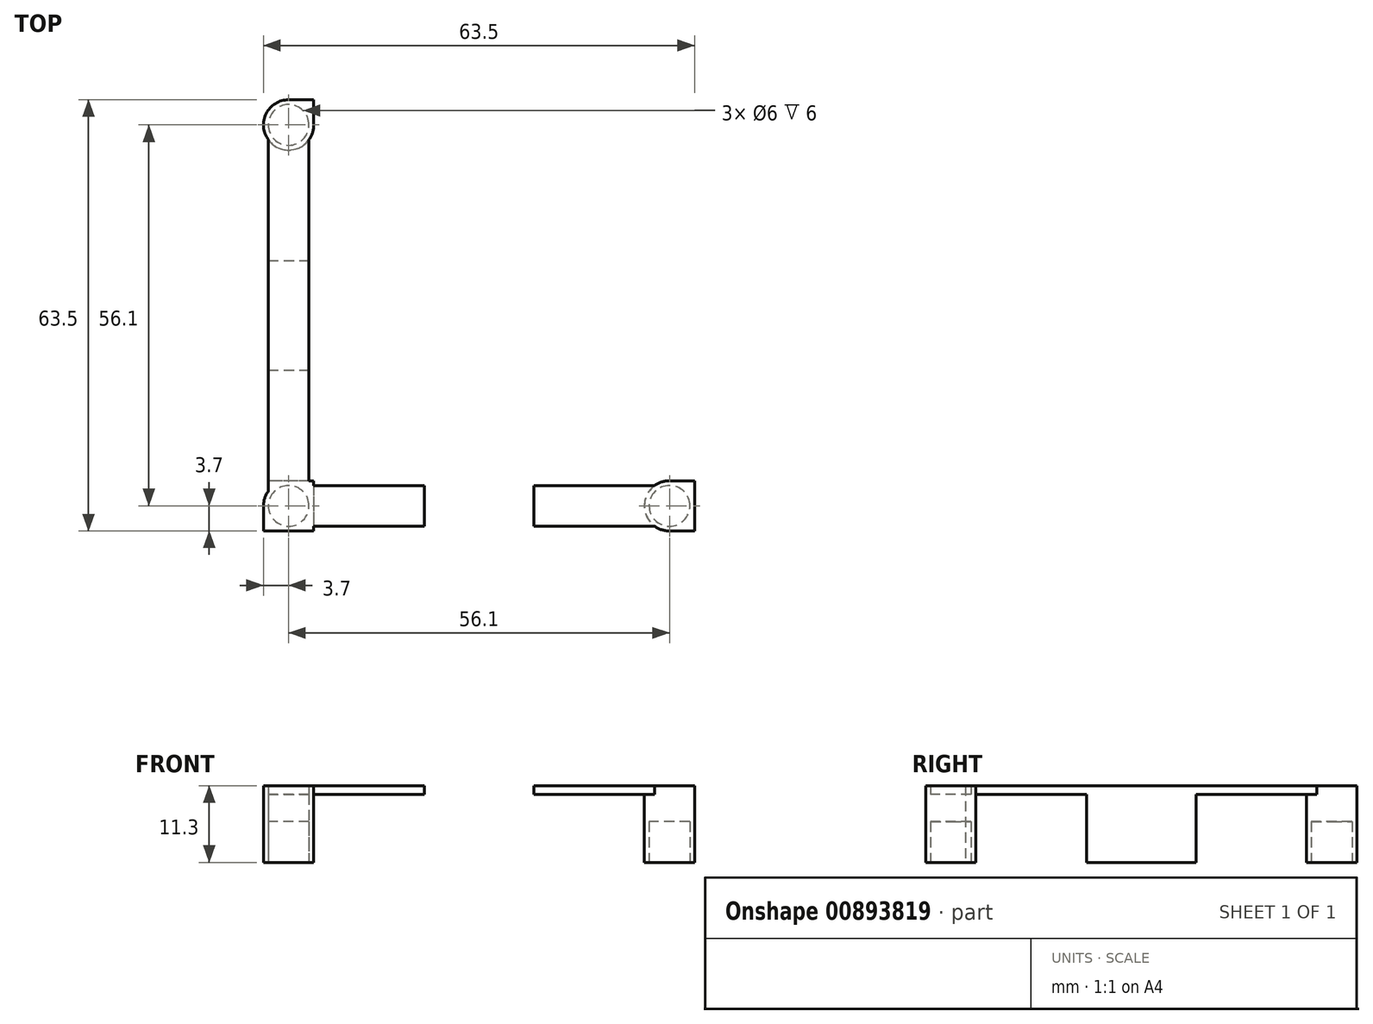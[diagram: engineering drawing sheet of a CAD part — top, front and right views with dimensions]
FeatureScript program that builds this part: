
annotation { "Feature Type Name" : "Feature", "Feature Type Description" : "" }
export const myFeature = defineFeature(function(context is Context, id is Id, definition is map)
    precondition{}
    {
        {
            var Q0;
            Q0=qCreatedBy(makeId("Top.planeOp"),FACE);
            var sketch = newSketch(context, id + "F0", { "sketchPlane" : qUnion([Q0])});
            skLineSegment(sketch, "E0.bottom", {"start": v(0, 0) * mm, "end": v(63.5, 0) * mm});
            skLineSegment(sketch, "E0.top", {"start": v(0, 63.5) * mm, "end": v(63.5, 63.5) * mm, "construction": true});
            skLineSegment(sketch, "E0.left", {"start": v(0, 0) * mm, "end": v(0, 63.5) * mm});
            skLineSegment(sketch, "E0.right", {"start": v(63.5, 0) * mm, "end": v(63.5, 63.5) * mm, "construction": true});
            skLineSegment(sketch, "E1", {"start": v(0, 63.5) * mm, "end": v(0, 0) * mm});
            skLineSegment(sketch, "E2.0", {"start": v(7.4, 7.4) * mm, "end": v(63.5, 7.4) * mm});
            skLineSegment(sketch, "E2.1", {"start": v(7.4, 63.5) * mm, "end": v(7.4, 7.4) * mm});
            skLineSegment(sketch, "E3", {"start": v(63.5, 7.4) * mm, "end": v(63.5, 0) * mm});
            skLineSegment(sketch, "E4", {"start": v(7.4, 63.5) * mm, "end": v(0, 63.5) * mm});
            skCircle(sketch, "E5", {"center": v(3.7, 59.8) * mm, "radius": 3 * mm});
            skCircle(sketch, "E6", {"center": v(59.8, 3.7) * mm, "radius": 3 * mm});
            skCircle(sketch, "E7", {"center": v(3.7, 3.7) * mm, "radius": 3 * mm});
            skLineSegment(sketch, "E8", {"start": v(3.7, 59.8) * mm, "end": v(7.4, 59.8) * mm, "construction": true});
            skLineSegment(sketch, "E9", {"start": v(7.4, 59.8) * mm, "end": v(0, 59.8) * mm, "construction": true});
            skLineSegment(sketch, "E10", {"start": v(3.7, 3.7) * mm, "end": v(3.7, 0) * mm, "construction": true});
            skLineSegment(sketch, "E11", {"start": v(3.7, 0) * mm, "end": v(3.7, 3.7) * mm, "construction": true});
            skLineSegment(sketch, "E12", {"start": v(3.7, 3.7) * mm, "end": v(0, 3.7) * mm, "construction": true});
            skLineSegment(sketch, "E13", {"start": v(3.7, 3.7) * mm, "end": v(6.7, 3.7) * mm, "construction": true});
            skLineSegment(sketch, "E14", {"start": v(59.8, 3.7) * mm, "end": v(59.8, 7.4) * mm, "construction": true});
            skLineSegment(sketch, "E15", {"start": v(59.8, 7.4) * mm, "end": v(59.8, 0) * mm, "construction": true});
            skLineSegment(sketch, "E16", {"start": v(3.7, 3.7) * mm, "end": v(3.7, 6.7) * mm, "construction": true});
            skLineSegment(sketch, "E17", {"start": v(59.8, 0.7) * mm, "end": v(3.7, 0.7) * mm});
            skLineSegment(sketch, "E18", {"start": v(59.8, 6.7) * mm, "end": v(3.7, 6.7) * mm});
            skLineSegment(sketch, "E19", {"start": v(6.7, 3.7) * mm, "end": v(6.7, 59.8) * mm});
            skLineSegment(sketch, "E20", {"start": v(0.7, 59.8) * mm, "end": v(0.7, 3.7) * mm});
            skLineSegment(sketch, "E21.bottom", {"start": v(0.7, 39.8) * mm, "end": v(6.7, 39.8) * mm});
            skLineSegment(sketch, "E21.top", {"start": v(0.7, 23.7) * mm, "end": v(6.7, 23.7) * mm});
            skLineSegment(sketch, "E21.left", {"start": v(0.7, 39.8) * mm, "end": v(0.7, 23.7) * mm});
            skLineSegment(sketch, "E21.right", {"start": v(6.7, 39.8) * mm, "end": v(6.7, 23.7) * mm});
            skLineSegment(sketch, "E22.bottom", {"start": v(23.7, 6.7) * mm, "end": v(39.8, 6.7) * mm});
            skLineSegment(sketch, "E22.top", {"start": v(23.7, 0.7) * mm, "end": v(39.8, 0.7) * mm});
            skLineSegment(sketch, "E22.left", {"start": v(23.7, 6.7) * mm, "end": v(23.7, 0.7) * mm});
            skLineSegment(sketch, "E22.right", {"start": v(39.8, 6.7) * mm, "end": v(39.8, 0.7) * mm});
            skCircle(sketch, "E23", {"center": v(3.7, 59.8) * mm, "radius": 3.7 * mm});
            skCircle(sketch, "E24", {"center": v(3.7, 3.7) * mm, "radius": 3.7 * mm});
            skCircle(sketch, "E25", {"center": v(59.8, 3.7) * mm, "radius": 3.7 * mm});
            skLineSegment(sketch, "E26", {"start": v(6.7, 3.7) * mm, "end": v(7.4, 3.7) * mm, "construction": true});
            skLineSegment(sketch, "E27", {"start": v(3.7, 6.7) * mm, "end": v(3.7, 7.4) * mm, "construction": true});
            skLineSegment(sketch, "E28", {"start": v(7.4, 7.4) * mm, "end": v(0, 7.4) * mm});
            skLineSegment(sketch, "E29", {"start": v(7.4, 7.4) * mm, "end": v(7.4, 0) * mm});
            skSolve(sketch);
        }
        {
            var Q0;
            {var subQ0=sQuery(id+"F0.wireOp",EDGE,"E6");var subQ1=makeQuery(id+"F0.imprint","INTERSECT",VERTEX,{"derivedFrom":[subQ0,sQuery(id+"F0.wireOp",EDGE,"E17")]});Q0=makeQuery(id+"F0.imprint","IMPRINT",FACE,{"disambiguationData":[TD([[makeQuery(id+"F0.imprint","IMPRINT",EDGE,{"disambiguationData":[TD([[subQ1,1.0]])],"derivedFrom":subQ0}),1.0]])]});}
            var Q1;
            {var subQ0=sQuery(id+"F0.wireOp",EDGE,"E22.top");Q1=makeQuery(id+"F0.imprint","IMPRINT",FACE,{"disambiguationData":[TD([[makeQuery(id+"F0.imprint","IMPRINT",EDGE,{"derivedFrom":subQ0}),-1.0]])]});}
            var Q2;
            {var subQ4=sQuery(id+"F0.wireOp",EDGE,"E7");var subQ6=sQuery(id+"F0.wireOp",EDGE,"E17");var subQ7=makeQuery(id+"F0.imprint","INTERSECT",VERTEX,{"derivedFrom":[subQ4,subQ6]});Q2=makeQuery(id+"F0.imprint","IMPRINT",FACE,{"disambiguationData":[TD([[makeQuery(id+"F0.imprint","IMPRINT",EDGE,{"disambiguationData":[TD([[subQ7,-1.0]])],"derivedFrom":subQ4}),-1.0]])]});}
            var Q3;
            {var subQ0=sQuery(id+"F0.wireOp",EDGE,"E19");var subQ1=sQuery(id+"F0.wireOp",EDGE,"E5");var subQ2=makeQuery(id+"F0.imprint","INTERSECT",VERTEX,{"derivedFrom":[subQ1,subQ0]});Q3=makeQuery(id+"F0.imprint","IMPRINT",FACE,{"disambiguationData":[TD([[makeQuery(id+"F0.imprint","IMPRINT",EDGE,{"disambiguationData":[TD([[subQ2,1.0]])],"derivedFrom":subQ1}),-1.0]])]});}
            var Q4;
            {var subQ0=sQuery(id+"F0.wireOp",EDGE,"E21.top");Q4=makeQuery(id+"F0.imprint","IMPRINT",FACE,{"disambiguationData":[TD([[makeQuery(id+"F0.imprint","IMPRINT",EDGE,{"derivedFrom":subQ0}),-1.0]])]});}
            var Q5;
            {var subQ0=sQuery(id+"F0.wireOp",EDGE,"E22.right");Q5=makeQuery(id+"F0.imprint","IMPRINT",FACE,{"disambiguationData":[TD([[makeQuery(id+"F0.imprint","IMPRINT",EDGE,{"derivedFrom":subQ0}),1.0]])]});}
            var Q6;
            {var subQ0=sQuery(id+"F0.wireOp",EDGE,"E18");var subQ1=sQuery(id+"F0.wireOp",EDGE,"E7");var subQ2=makeQuery(id+"F0.imprint","INTERSECT",VERTEX,{"derivedFrom":[subQ1,subQ0]});Q6=makeQuery(id+"F0.imprint","IMPRINT",FACE,{"disambiguationData":[TD([[makeQuery(id+"F0.imprint","IMPRINT",EDGE,{"disambiguationData":[TD([[subQ2,1.0]])],"derivedFrom":subQ1}),-1.0]])]});}
            var Q7;
            {var subQ0=sQuery(id+"F0.wireOp",EDGE,"E21.right");Q7=makeQuery(id+"F0.imprint","IMPRINT",FACE,{"disambiguationData":[TD([[makeQuery(id+"F0.imprint","IMPRINT",EDGE,{"derivedFrom":subQ0}),1.0]])]});}
            var Q8;
            {var subQ4=sQuery(id+"F0.wireOp",EDGE,"E6");var subQ7=sQuery(id+"F0.wireOp",EDGE,"E17");var subQ8=makeQuery(id+"F0.imprint","INTERSECT",VERTEX,{"derivedFrom":[subQ4,subQ7]});Q8=makeQuery(id+"F0.imprint","IMPRINT",FACE,{"disambiguationData":[TD([[makeQuery(id+"F0.imprint","IMPRINT",EDGE,{"disambiguationData":[TD([[subQ8,-1.0]])],"derivedFrom":subQ4}),-1.0]])]});}
            var Q9;
            {var subQ0=sQuery(id+"F0.wireOp",EDGE,"E4");var subQ1=sQuery(id+"F0.wireOp",EDGE,"E1");var subQ2=makeQuery(id+"F0.imprint","INTERSECT",VERTEX,{"derivedFrom":[subQ1,subQ0]});Q9=makeQuery(id+"F0.imprint","IMPRINT",FACE,{"disambiguationData":[TD([[makeQuery(id+"F0.imprint","IMPRINT",EDGE,{"disambiguationData":[TD([[subQ2,-1.0]])],"derivedFrom":subQ1}),1.0]])]});}
            var Q10;
            {var subQ0=sQuery(id+"F0.wireOp",EDGE,"E3");var subQ1=sQuery(id+"F0.wireOp",EDGE,"E0.bottom");var subQ2=makeQuery(id+"F0.imprint","INTERSECT",VERTEX,{"derivedFrom":[subQ1,subQ0]});Q10=makeQuery(id+"F0.imprint","IMPRINT",FACE,{"disambiguationData":[TD([[makeQuery(id+"F0.imprint","IMPRINT",EDGE,{"disambiguationData":[TD([[subQ2,1.0]])],"derivedFrom":subQ1}),1.0]])]});}
            var Q11;
            {var subQ0=sQuery(id+"F0.wireOp",EDGE,"E4");var subQ1=sQuery(id+"F0.wireOp",EDGE,"E2.1");var subQ2=makeQuery(id+"F0.imprint","INTERSECT",VERTEX,{"derivedFrom":[subQ1,subQ0]});Q11=makeQuery(id+"F0.imprint","IMPRINT",FACE,{"disambiguationData":[TD([[makeQuery(id+"F0.imprint","IMPRINT",EDGE,{"disambiguationData":[TD([[subQ2,-1.0]])],"derivedFrom":subQ1}),-1.0]])]});}
            var Q12;
            {var subQ0=sQuery(id+"F0.wireOp",EDGE,"E3");var subQ1=sQuery(id+"F0.wireOp",EDGE,"E2.0");var subQ2=makeQuery(id+"F0.imprint","INTERSECT",VERTEX,{"derivedFrom":[subQ1,subQ0]});Q12=makeQuery(id+"F0.imprint","IMPRINT",FACE,{"disambiguationData":[TD([[makeQuery(id+"F0.imprint","IMPRINT",EDGE,{"disambiguationData":[TD([[subQ2,1.0]])],"derivedFrom":subQ1}),-1.0]])]});}
            var Q13;
            {var subQ0=sQuery(id+"F0.wireOp",EDGE,"E21.left");Q13=makeQuery(id+"F0.imprint","IMPRINT",FACE,{"disambiguationData":[TD([[makeQuery(id+"F0.imprint","IMPRINT",EDGE,{"derivedFrom":subQ0}),-1.0]])]});}
            var Q14;
            {var subQ0=sQuery(id+"F0.wireOp",EDGE,"E17");var subQ1=sQuery(id+"F0.wireOp",EDGE,"E6");var subQ2=makeQuery(id+"F0.imprint","INTERSECT",VERTEX,{"derivedFrom":[subQ1,subQ0]});Q14=makeQuery(id+"F0.imprint","IMPRINT",FACE,{"disambiguationData":[TD([[makeQuery(id+"F0.imprint","IMPRINT",EDGE,{"disambiguationData":[TD([[subQ2,1.0]])],"derivedFrom":subQ1}),-1.0]])]});}
            var Q15;
            {var subQ0=sQuery(id+"F0.wireOp",EDGE,"E21.bottom");Q15=makeQuery(id+"F0.imprint","IMPRINT",FACE,{"disambiguationData":[TD([[makeQuery(id+"F0.imprint","IMPRINT",EDGE,{"derivedFrom":subQ0}),1.0]])]});}
            var Q16;
            {var subQ4=sQuery(id+"F0.wireOp",EDGE,"E22.left");Q16=makeQuery(id+"F0.imprint","IMPRINT",FACE,{"disambiguationData":[TD([[makeQuery(id+"F0.imprint","IMPRINT",EDGE,{"derivedFrom":subQ4}),-1.0]])]});}
            var Q17;
            {var subQ1=sQuery(id+"F0.wireOp",EDGE,"E7");var subQ5=sQuery(id+"F0.wireOp",EDGE,"E18");var subQ6=makeQuery(id+"F0.imprint","INTERSECT",VERTEX,{"derivedFrom":[subQ1,subQ5]});Q17=makeQuery(id+"F0.imprint","IMPRINT",FACE,{"disambiguationData":[TD([[makeQuery(id+"F0.imprint","IMPRINT",EDGE,{"disambiguationData":[TD([[subQ6,-1.0]])],"derivedFrom":subQ1}),-1.0]])]});}
            var Q18;
            Q18=makeQuery(id+"F0.imprint","IMPRINT",FACE,{"disambiguationData":[TD([[makeQuery(id+"F0.imprint","IMPRINT",EDGE,{"derivedFrom":sQuery(id+"F0.wireOp",EDGE,"E22.bottom")}),-1.0]])]});
            var Q19;
            {var subQ0=sQuery(id+"F0.wireOp",EDGE,"E5");var subQ1=makeQuery(id+"F0.imprint","INTERSECT",VERTEX,{"derivedFrom":[subQ0,sQuery(id+"F0.wireOp",EDGE,"E19")]});Q19=makeQuery(id+"F0.imprint","IMPRINT",FACE,{"disambiguationData":[TD([[makeQuery(id+"F0.imprint","IMPRINT",EDGE,{"disambiguationData":[TD([[subQ1,-1.0]])],"derivedFrom":subQ0}),1.0]])]});}
            var Q20;
            {var subQ1=sQuery(id+"F0.wireOp",EDGE,"E7");var subQ6=sQuery(id+"F0.wireOp",EDGE,"E17");var subQ7=makeQuery(id+"F0.imprint","INTERSECT",VERTEX,{"derivedFrom":[subQ1,subQ6]});Q20=makeQuery(id+"F0.imprint","IMPRINT",FACE,{"disambiguationData":[TD([[makeQuery(id+"F0.imprint","IMPRINT",EDGE,{"disambiguationData":[TD([[subQ7,1.0]])],"derivedFrom":subQ1}),-1.0]])]});}
            var Q21;
            {var subQ3=sQuery(id+"F0.wireOp",EDGE,"E19");var subQ4=sQuery(id+"F0.wireOp",EDGE,"E5");var subQ5=makeQuery(id+"F0.imprint","INTERSECT",VERTEX,{"derivedFrom":[subQ4,subQ3]});Q21=makeQuery(id+"F0.imprint","IMPRINT",FACE,{"disambiguationData":[TD([[makeQuery(id+"F0.imprint","IMPRINT",EDGE,{"disambiguationData":[TD([[subQ5,-1.0]])],"derivedFrom":subQ4}),-1.0]])]});}
            var Q22;
            Q22=makeQuery(id+"F0.imprint","IMPRINT",FACE,{"disambiguationData":[TD([[makeQuery(id+"F0.imprint","IMPRINT",EDGE,{"derivedFrom":sQuery(id+"F0.wireOp",EDGE,"E21.bottom")}),-1.0]])]});
            var Q23;
            {var subQ0=sQuery(id+"F0.wireOp",EDGE,"E7");var subQ1=makeQuery(id+"F0.imprint","INTERSECT",VERTEX,{"derivedFrom":[subQ0,sQuery(id+"F0.wireOp",EDGE,"E18")]});Q23=makeQuery(id+"F0.imprint","IMPRINT",FACE,{"disambiguationData":[TD([[makeQuery(id+"F0.imprint","IMPRINT",EDGE,{"disambiguationData":[TD([[subQ1,1.0]])],"derivedFrom":subQ0}),1.0]])]});}
            var Q24;
            {var subQ0=sQuery(id+"F0.wireOp",EDGE,"E1");var subQ1=sQuery(id+"F0.wireOp",EDGE,"E0.bottom");var subQ2=makeQuery(id+"F0.imprint","INTERSECT",VERTEX,{"derivedFrom":[subQ1,subQ0]});Q24=makeQuery(id+"F0.imprint","IMPRINT",FACE,{"disambiguationData":[TD([[makeQuery(id+"F0.imprint","IMPRINT",EDGE,{"disambiguationData":[TD([[subQ2,-1.0]])],"derivedFrom":subQ1}),1.0]])]});}
            var Q25;
            {var subQ0=sQuery(id+"F0.wireOp",EDGE,"E19");var subQ1=sQuery(id+"F0.wireOp",EDGE,"E18");var subQ2=makeQuery(id+"F0.imprint","INTERSECT",VERTEX,{"derivedFrom":[subQ1,subQ0]});Q25=makeQuery(id+"F0.imprint","IMPRINT",FACE,{"disambiguationData":[TD([[makeQuery(id+"F0.imprint","IMPRINT",EDGE,{"disambiguationData":[TD([[subQ2,-1.0]])],"derivedFrom":subQ1}),1.0]])]});}
            var Q26;
            {var subQ0=sQuery(id+"F0.wireOp",EDGE,"E22.bottom");Q26=makeQuery(id+"F0.imprint","IMPRINT",FACE,{"disambiguationData":[TD([[makeQuery(id+"F0.imprint","IMPRINT",EDGE,{"derivedFrom":subQ0}),1.0]])]});}
            var Q27;
            {var subQ0=sQuery(id+"F0.wireOp",EDGE,"E29");var subQ1=sQuery(id+"F0.wireOp",EDGE,"E0.bottom");var subQ2=makeQuery(id+"F0.imprint","INTERSECT",VERTEX,{"derivedFrom":[subQ1,subQ0]});Q27=makeQuery(id+"F0.imprint","IMPRINT",FACE,{"disambiguationData":[TD([[makeQuery(id+"F0.imprint","IMPRINT",EDGE,{"disambiguationData":[TD([[subQ2,1.0]])],"derivedFrom":subQ1}),1.0]])]});}
            var Q28;
            {var subQ0=sQuery(id+"F0.wireOp",EDGE,"E28");var subQ1=sQuery(id+"F0.wireOp",EDGE,"E20");var subQ2=makeQuery(id+"F0.imprint","INTERSECT",VERTEX,{"derivedFrom":[subQ1,subQ0]});Q28=makeQuery(id+"F0.imprint","IMPRINT",FACE,{"disambiguationData":[TD([[makeQuery(id+"F0.imprint","IMPRINT",EDGE,{"disambiguationData":[TD([[subQ2,-1.0]])],"derivedFrom":subQ1}),1.0]])]});}
            var Q29;
            {var subQ0=sQuery(id+"F0.wireOp",EDGE,"E28");var subQ1=sQuery(id+"F0.wireOp",EDGE,"E1");var subQ2=makeQuery(id+"F0.imprint","INTERSECT",VERTEX,{"derivedFrom":[subQ1,subQ0]});Q29=makeQuery(id+"F0.imprint","IMPRINT",FACE,{"disambiguationData":[TD([[makeQuery(id+"F0.imprint","IMPRINT",EDGE,{"disambiguationData":[TD([[subQ2,-1.0]])],"derivedFrom":subQ1}),1.0]])]});}
            var Q30;
            {var subQ0=sQuery(id+"F0.wireOp",EDGE,"E19");var subQ1=sQuery(id+"F0.wireOp",EDGE,"E18");var subQ2=makeQuery(id+"F0.imprint","INTERSECT",VERTEX,{"derivedFrom":[subQ1,subQ0]});Q30=makeQuery(id+"F0.imprint","IMPRINT",FACE,{"disambiguationData":[TD([[makeQuery(id+"F0.imprint","IMPRINT",EDGE,{"disambiguationData":[TD([[subQ2,-1.0]])],"derivedFrom":subQ1}),-1.0]])]});}
            var Q31;
            {var subQ0=sQuery(id+"F0.wireOp",EDGE,"E29");var subQ1=sQuery(id+"F0.wireOp",EDGE,"E17");var subQ2=makeQuery(id+"F0.imprint","INTERSECT",VERTEX,{"derivedFrom":[subQ1,subQ0]});Q31=makeQuery(id+"F0.imprint","IMPRINT",FACE,{"disambiguationData":[TD([[makeQuery(id+"F0.imprint","IMPRINT",EDGE,{"disambiguationData":[TD([[subQ2,-1.0]])],"derivedFrom":subQ1}),-1.0]])]});}
            var Q32;
            {var subQ0=sQuery(id+"F0.wireOp",EDGE,"E29");var subQ1=sQuery(id+"F0.wireOp",EDGE,"E18");var subQ2=makeQuery(id+"F0.imprint","INTERSECT",VERTEX,{"derivedFrom":[subQ1,subQ0]});Q32=makeQuery(id+"F0.imprint","IMPRINT",FACE,{"disambiguationData":[TD([[makeQuery(id+"F0.imprint","IMPRINT",EDGE,{"disambiguationData":[TD([[subQ2,-1.0]])],"derivedFrom":subQ1}),1.0]])]});}
            var Q33;
            {var subQ0=sQuery(id+"F0.wireOp",EDGE,"E29");var subQ1=sQuery(id+"F0.wireOp",EDGE,"E18");var subQ2=makeQuery(id+"F0.imprint","INTERSECT",VERTEX,{"derivedFrom":[subQ1,subQ0]});Q33=makeQuery(id+"F0.imprint","IMPRINT",FACE,{"disambiguationData":[TD([[makeQuery(id+"F0.imprint","IMPRINT",EDGE,{"disambiguationData":[TD([[subQ2,-1.0]])],"derivedFrom":subQ1}),-1.0]])]});}
            extrude(context, id + "F1", {"entities" : qUnion([Q0, Q1, Q2, Q3, Q4, Q5, Q6, Q7, Q8, Q9, Q10, Q11, Q12, Q13, Q14, Q15, Q16, Q17, Q18, Q19, Q20, Q21, Q22, Q23, Q24, Q25, Q26, Q27, Q28, Q29, Q30, Q31, Q32, Q33]), "depth" : 11.3 * mm, "offsetDistance" : 25 * mm});
        }
        {
            var Q0;
            {var subQ0=sQuery(id+"F0.wireOp",EDGE,"E5");var subQ1=makeQuery(id+"F0.imprint","INTERSECT",VERTEX,{"derivedFrom":[subQ0,sQuery(id+"F0.wireOp",EDGE,"E19")]});Q0=makeQuery(id+"F0.imprint","IMPRINT",FACE,{"disambiguationData":[TD([[makeQuery(id+"F0.imprint","IMPRINT",EDGE,{"disambiguationData":[TD([[subQ1,-1.0]])],"derivedFrom":subQ0}),1.0]])]});}
            var Q1;
            {var subQ0=sQuery(id+"F0.wireOp",EDGE,"E7");var subQ1=makeQuery(id+"F0.imprint","INTERSECT",VERTEX,{"derivedFrom":[subQ0,sQuery(id+"F0.wireOp",EDGE,"E18")]});Q1=makeQuery(id+"F0.imprint","IMPRINT",FACE,{"disambiguationData":[TD([[makeQuery(id+"F0.imprint","IMPRINT",EDGE,{"disambiguationData":[TD([[subQ1,1.0]])],"derivedFrom":subQ0}),1.0]])]});}
            var Q2;
            {var subQ0=sQuery(id+"F0.wireOp",EDGE,"E6");var subQ1=makeQuery(id+"F0.imprint","INTERSECT",VERTEX,{"derivedFrom":[subQ0,sQuery(id+"F0.wireOp",EDGE,"E17")]});Q2=makeQuery(id+"F0.imprint","IMPRINT",FACE,{"disambiguationData":[TD([[makeQuery(id+"F0.imprint","IMPRINT",EDGE,{"disambiguationData":[TD([[subQ1,1.0]])],"derivedFrom":subQ0}),1.0]])]});}
            extrude(context, id + "F2", {"entities" : qUnion([Q0, Q1, Q2]), "operationType" : NewBodyOperationType.REMOVE, "depth" : 6 * mm, "offsetDistance" : 25 * mm});
        }
        {
            var Q0;
            {var subQ0=sQuery(id+"F0.wireOp",EDGE,"E21.bottom");Q0=makeQuery(id+"F0.imprint","IMPRINT",FACE,{"disambiguationData":[TD([[makeQuery(id+"F0.imprint","IMPRINT",EDGE,{"derivedFrom":subQ0}),1.0]])]});}
            var Q1;
            {var subQ0=sQuery(id+"F0.wireOp",EDGE,"E21.top");Q1=makeQuery(id+"F0.imprint","IMPRINT",FACE,{"disambiguationData":[TD([[makeQuery(id+"F0.imprint","IMPRINT",EDGE,{"derivedFrom":subQ0}),-1.0]])]});}
            var Q2;
            {var subQ0=sQuery(id+"F0.wireOp",EDGE,"E22.right");Q2=makeQuery(id+"F0.imprint","IMPRINT",FACE,{"disambiguationData":[TD([[makeQuery(id+"F0.imprint","IMPRINT",EDGE,{"derivedFrom":subQ0}),1.0]])]});}
            var Q3;
            {var subQ4=sQuery(id+"F0.wireOp",EDGE,"E22.left");Q3=makeQuery(id+"F0.imprint","IMPRINT",FACE,{"disambiguationData":[TD([[makeQuery(id+"F0.imprint","IMPRINT",EDGE,{"derivedFrom":subQ4}),-1.0]])]});}
            extrude(context, id + "F3", {"entities" : qUnion([Q0, Q1, Q2, Q3]), "operationType" : NewBodyOperationType.REMOVE, "depth" : 10 * mm, "offsetDistance" : 25 * mm});
        }
    });
